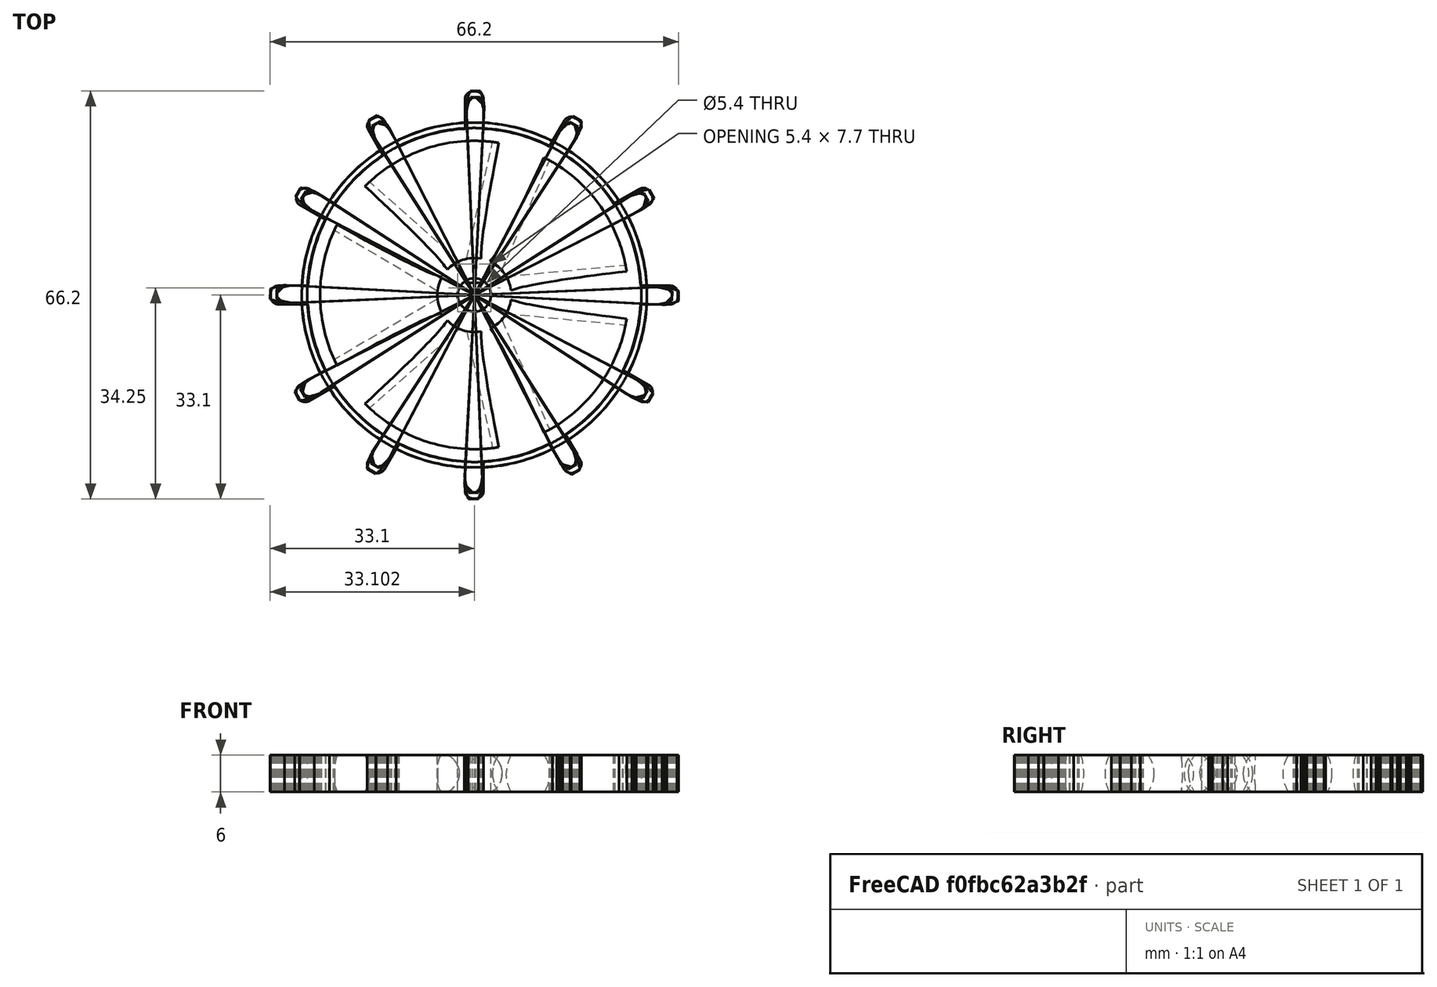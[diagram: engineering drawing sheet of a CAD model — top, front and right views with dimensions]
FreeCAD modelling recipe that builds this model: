
FCSTD DOCUMENT  (FreeCAD 0.17R13541 (Git))
Label: gear_fullcircle
License: All rights reserved
LicenseURL: http://en.wikipedia.org/wiki/All_rights_reserved
objects: Part::MultiFuse×22, Part::Cylinder×10, Part::Cut×7, Part::Chamfer×6, Part::Fillet×6, Part::Box×5, Part::Feature×2, Part::Extrusion×2, Part::Cone×1
note: 61 computed .brp shape members not serialized (recipe doc carries the construction recipe); baked Part::Feature solids carry a one-line shape summary decoded from their .brp

FEATURE [Part::Feature] GearFlat
  shape: bbox 64.12 x 64.12 x 2.5e-07 mm, 36 faces, 0 solids (baked)
FEATURE [Part::Extrusion] Gear3D
  Base = -> GearFlat
  Dir = (0,0,6)
  DirMode = 0
  FaceMakerClass = Part::FaceMakerExtrusion
  LengthFwd = 0
  LengthRev = 0
  Placement = pos=(0,0,0) rot=(0,0,-1;0.05236rad)
  Solid = false
  Symmetric = false
FEATURE [Part::Box] Box
  AttacherType = Attacher::AttachEngine3D
  Height = 6
  Length = 3
  Placement = pos=(-1.5,-32,0) rot=(0,0,1;0rad)
  Width = 64
FEATURE [Part::Chamfer] Chamfer
  Base = -> Box
  Edges = 4 edges r=1.2: [Edge1,Edge3,Edge5,Edge7]
FEATURE [Part::Chamfer] Chamfer001
  Base = -> Box
  Edges = 4 edges r=1.2: [Edge1,Edge3,Edge5,Edge7]
  Placement = pos=(0,0,0) rot=(0,0,1;0.523599rad)
FEATURE [Part::Chamfer] Chamfer002
  Base = -> Box
  Edges = 4 edges r=1.2: [Edge1,Edge3,Edge5,Edge7]
  Placement = pos=(0,0,0) rot=(0,0,1;1.0472rad)
FEATURE [Part::Chamfer] Chamfer003
  Base = -> Box
  Edges = 4 edges r=1.2: [Edge1,Edge3,Edge5,Edge7]
  Placement = pos=(0,0,0) rot=(0,0,1;1.5708rad)
FEATURE [Part::Chamfer] Chamfer004
  Base = -> Box
  Edges = 4 edges r=1.2: [Edge1,Edge3,Edge5,Edge7]
  Placement = pos=(0,0,0) rot=(0,0,1;2.0944rad)
FEATURE [Part::Chamfer] Chamfer005
  Base = -> Box
  Edges = 4 edges r=1.2: [Edge1,Edge3,Edge5,Edge7]
  Placement = pos=(0,0,0) rot=(0,0,1;2.61799rad)
FEATURE [Part::MultiFuse] Fusion
  Shapes = -> [Chamfer,Chamfer001]
FEATURE [Part::MultiFuse] Fusion001
  Shapes = -> [Chamfer005,Fusion]
FEATURE [Part::MultiFuse] Fusion002
  Shapes = -> [Chamfer004,Fusion001]
FEATURE [Part::MultiFuse] Fusion003
  Shapes = -> [Chamfer003,Fusion002]
FEATURE [Part::MultiFuse] Fusion004
  Shapes = -> [Chamfer002,Fusion003]
FEATURE [Part::Cylinder] Cylinder
  Angle = 360
  AttacherType = Attacher::AttachEngine3D
  Height = 6
  Radius = 27
FEATURE [Part::Cylinder] Cylinder001
  Angle = 360
  AttacherType = Attacher::AttachEngine3D
  Height = 6
  Radius = 23
FEATURE [Part::Cut] Cut
  Base = -> Fusion004
  Tool = -> Cylinder001
FEATURE [Part::MultiFuse] Fusion005
  Shapes = -> [Cut,Cylinder]
FEATURE [Part::Cylinder] Cylinder002
  Angle = 360
  AttacherType = Attacher::AttachEngine3D
  Height = 6
  Radius = 2.7
FEATURE [Part::Cut] Cut001
  Base = -> Fusion005
  Tool = -> Cylinder002
FEATURE [Part::Box] Box001
  AttacherType = Attacher::AttachEngine3D
  Height = 6
  Length = 3
  Placement = pos=(-1.5,2,0) rot=(0,0,1;0rad)
  Width = 3
FEATURE [Part::MultiFuse] Fusion006
  Shapes = -> [Cut001,Box001]
FEATURE [Part::Feature] GearFlat001
  shape: bbox 66.19 x 66.19 x 2.5e-07 mm, 36 faces, 0 solids (baked)
FEATURE [Part::Extrusion] Gear3D001
  Base = -> GearFlat001
  Dir = (0,0,6)
  DirMode = 0
  FaceMakerClass = Part::FaceMakerExtrusion
  LengthFwd = 0
  LengthRev = 0
  Placement = pos=(0,0,0) rot=(0,0,-1;0.05236rad)
  Solid = false
  Symmetric = false
FEATURE [Part::Box] Box002
  AttacherType = Attacher::AttachEngine3D
  Height = 6
  Length = 3
  Placement = pos=(-1.5,-33,0) rot=(0,0,1;0rad)
  Width = 66
FEATURE [Part::Fillet] Fillet
  Base = -> Box002
  Edges = 4 edges r=1.2: [Edge1,Edge3,Edge5,Edge7]
FEATURE [Part::Fillet] Fillet001
  Base = -> Box002
  Edges = 4 edges r=1.2: [Edge1,Edge3,Edge5,Edge7]
  Placement = pos=(0,0,0) rot=(0,0,1;0.523599rad)
FEATURE [Part::Fillet] Fillet002
  Base = -> Box002
  Edges = 4 edges r=1.2: [Edge1,Edge3,Edge5,Edge7]
  Placement = pos=(0,0,0) rot=(0,0,1;1.0472rad)
FEATURE [Part::Fillet] Fillet003
  Base = -> Box002
  Edges = 4 edges r=1.2: [Edge1,Edge3,Edge5,Edge7]
  Placement = pos=(0,0,0) rot=(0,0,1;1.5708rad)
FEATURE [Part::Fillet] Fillet004
  Base = -> Box002
  Edges = 4 edges r=1.2: [Edge1,Edge3,Edge5,Edge7]
  Placement = pos=(0,0,0) rot=(0,0,1;2.0944rad)
FEATURE [Part::Fillet] Fillet005
  Base = -> Box002
  Edges = 4 edges r=1.2: [Edge1,Edge3,Edge5,Edge7]
  Placement = pos=(0,0,0) rot=(0,0,1;2.61799rad)
FEATURE [Part::Cylinder] Cylinder003
  Angle = 360
  AttacherType = Attacher::AttachEngine3D
  Height = 6
  Radius = 28
FEATURE [Part::MultiFuse] Fusion007
  Shapes = -> [Fillet,Fillet001]
FEATURE [Part::MultiFuse] Fusion008
  Shapes = -> [Fillet002,Fillet003]
FEATURE [Part::MultiFuse] Fusion009
  Shapes = -> [Fillet004,Fillet005]
FEATURE [Part::MultiFuse] Fusion010
  Shapes = -> [Fusion007,Fusion008]
FEATURE [Part::MultiFuse] Fusion011
  Shapes = -> [Fusion009,Fusion010]
FEATURE [Part::Cylinder] Cylinder003001
  Angle = 360
  AttacherType = Attacher::AttachEngine3D
  Height = 6
  Radius = 25
FEATURE [Part::Cut] Cut002
  Base = -> Fusion011
  Tool = -> Cylinder003001
FEATURE [Part::Cylinder] Cylinder003002
  Angle = 360
  AttacherType = Attacher::AttachEngine3D
  Height = 6
  Radius = 25
FEATURE [Part::MultiFuse] Fusion012
  Shapes = -> [Cylinder003,Cut002]
FEATURE [Part::Cut] Cut003
  Base = -> Fusion012
  Tool = -> Cylinder003002
FEATURE [Part::Cylinder] Cylinder003003
  Angle = 360
  AttacherType = Attacher::AttachEngine3D
  Height = 6
  Radius = 6
FEATURE [Part::Cylinder] Cylinder003003001
  Angle = 360
  AttacherType = Attacher::AttachEngine3D
  Height = 10
  Radius = 2.7
FEATURE [Part::Cut] Cut004
  Base = -> Cylinder003003
  Tool = -> Cylinder003003001
FEATURE [Part::Cone] Cone
  Angle = 360
  AttacherType = Attacher::AttachEngine3D
  Height = 21
  Placement = pos=(5,0,3) rot=(0,1,0;1.5708rad)
  Radius1 = 3
  Radius2 = 5
FEATURE [Part::Cylinder] Cylinder003003002
  Angle = 360
  AttacherType = Attacher::AttachEngine3D
  Height = 10
  Radius = 2
FEATURE [Part::MultiFuse] Fusion013001
  Shapes = -> [Cylinder003003002,Cone]
FEATURE [Part::MultiFuse] Fusion013002
  Placement = pos=(0,0,0) rot=(0,0,1;1.25664rad)
  Shapes = -> [Cylinder003003002,Cone]
FEATURE [Part::MultiFuse] Fusion013003
  Placement = pos=(0,0,0) rot=(0,0,1;2.51327rad)
  Shapes = -> [Cylinder003003002,Cone]
FEATURE [Part::MultiFuse] Fusion013004
  Placement = pos=(0,0,0) rot=(0,0,1;3.76991rad)
  Shapes = -> [Cylinder003003002,Cone]
FEATURE [Part::MultiFuse] Fusion013005
  Placement = pos=(0,0,0) rot=(0,0,-1;1.25664rad)
  Shapes = -> [Cylinder003003002,Cone]
FEATURE [Part::MultiFuse] Fusion013006
  Shapes = -> [Fusion013001,Fusion013003,Fusion013002,Fusion013004,Fusion013005]
FEATURE [Part::Cylinder] Cylinder003003003
  Angle = 360
  AttacherType = Attacher::AttachEngine3D
  Height = 10
  Radius = 2
FEATURE [Part::Cut] Cut005
  Base = -> Fusion013006
  Tool = -> Cylinder003003003
FEATURE [Part::Box] Box004
  AttacherType = Attacher::AttachEngine3D
  Height = 5
  Length = 100
  Placement = pos=(-50,-50,6) rot=(0,0,1;0rad)
  Width = 100
FEATURE [Part::Box] Box004001
  AttacherType = Attacher::AttachEngine3D
  Height = 5
  Length = 100
  Placement = pos=(-50,-50,-5) rot=(0,0,1;0rad)
  Width = 100
FEATURE [Part::MultiFuse] Fusion013007
  Shapes = -> [Box004,Box004001]
FEATURE [Part::MultiFuse] Fusion013008
  Shapes = -> [Cut003,Cut004]
FEATURE [Part::Cut] Cut006
  Base = -> Cut005
  Tool = -> Fusion013007
FEATURE [Part::MultiFuse] Fusion013010
  Shapes = -> [Fusion013008,Cut006]
